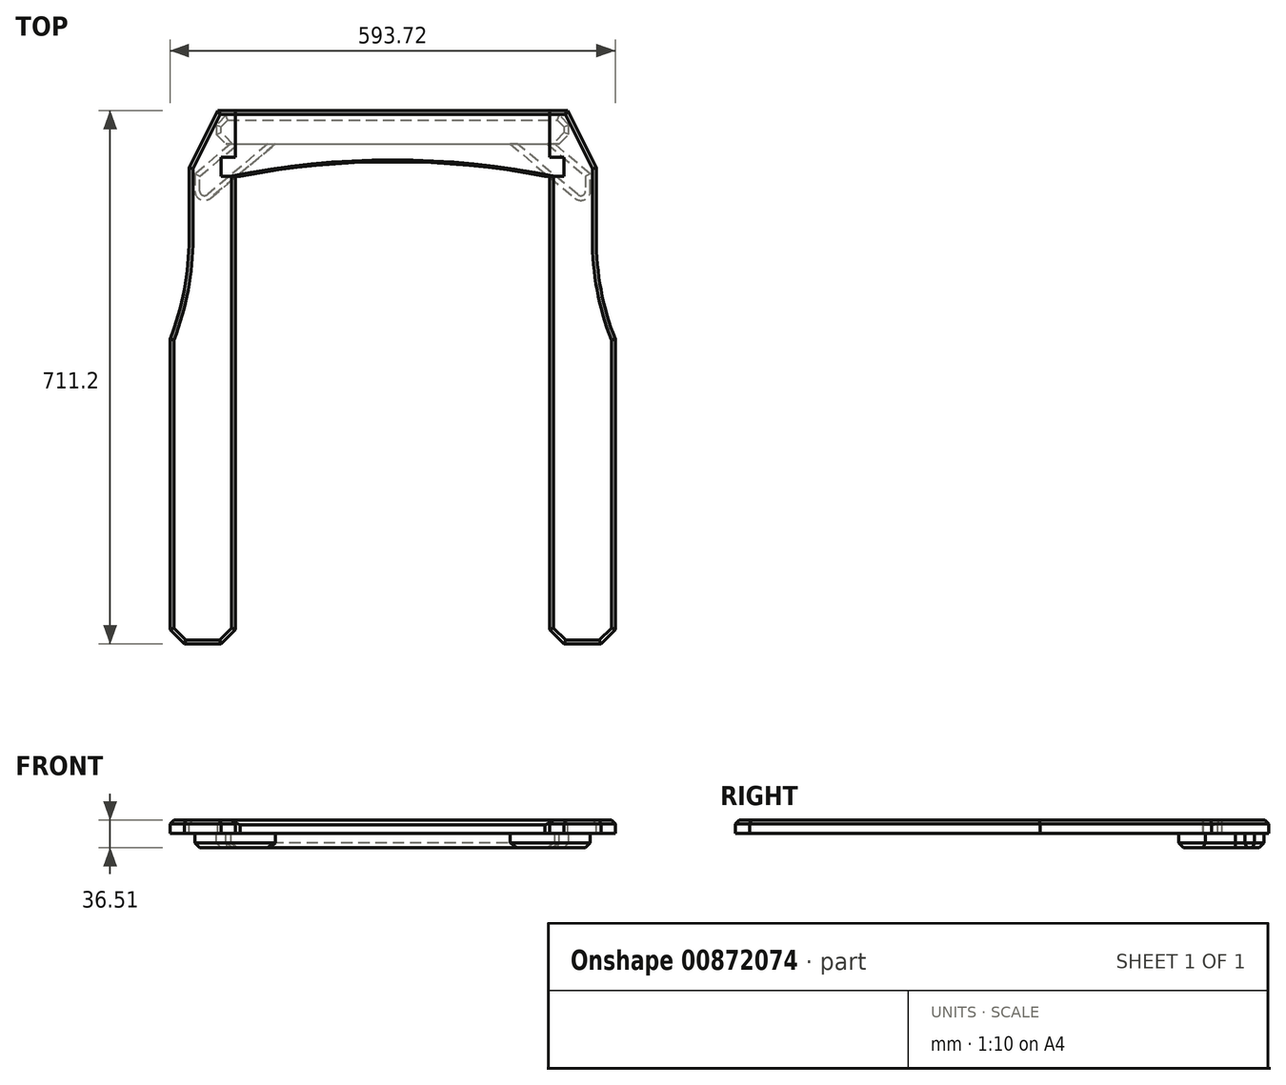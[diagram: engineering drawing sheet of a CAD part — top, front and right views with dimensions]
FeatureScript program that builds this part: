
annotation { "Feature Type Name" : "Feature", "Feature Type Description" : "" }
export const myFeature = defineFeature(function(context is Context, id is Id, definition is map)
    precondition{}
    {
        {
            var Q0;
            Q0=qCreatedBy(makeId("Top.planeOp"),FACE);
            var sketch = newSketch(context, id + "F0", { "sketchPlane" : qUnion([Q0])});
            skLineSegment(sketch, "E0.bottom", {"start": v(0, 0) * mm, "end": v(25.4, 0) * mm});
            skLineSegment(sketch, "E1", {"start": v(25.4, 18.53) * mm, "end": v(25.4, 0.79) * mm, "construction": true});
            skLineSegment(sketch, "E2", {"start": v(431.8, 17.8) * mm, "end": v(431.8, 0) * mm, "construction": true});
            skLineSegment(sketch, "E3", {"start": v(25.4, 0.79) * mm, "end": v(25.4, -24.2) * mm, "construction": true});
            skLineSegment(sketch, "E4", {"start": v(431.8, 0) * mm, "end": v(431.8, -25.28) * mm, "construction": true});
            skLineSegment(sketch, "E5", {"start": v(25.4, 0) * mm, "end": v(431.8, 0) * mm, "construction": true});
            skLineSegment(sketch, "E6", {"start": v(431.8, 0) * mm, "end": v(457.2, 0) * mm});
            skLineSegment(sketch, "E7", {"start": v(228.6, 19.05) * mm, "end": v(228.6, 0) * mm, "construction": true});
            skPoint(sketch, "E7.startSnap0", {"position": v(228.6, 0) * mm});
            skArc(sketch, "E8", {"start": v(431.8, 0) * mm, "mid": v(228.6, 19.05) * mm, "end": v(25.4, 0) * mm});
            skLineSegment(sketch, "E9", {"start": v(0, 0) * mm, "end": v(0, 25.4) * mm});
            skLineSegment(sketch, "E10", {"start": v(0, 25.4) * mm, "end": v(19.05, 25.4) * mm});
            skLineSegment(sketch, "E11", {"start": v(19.05, 25.4) * mm, "end": v(19.05, 87.31) * mm});
            skLineSegment(sketch, "E12", {"start": v(19.05, 87.31) * mm, "end": v(438.15, 87.31) * mm});
            skLineSegment(sketch, "E13", {"start": v(438.15, 87.31) * mm, "end": v(438.15, 25.4) * mm});
            skLineSegment(sketch, "E14", {"start": v(438.15, 25.4) * mm, "end": v(457.2, 25.4) * mm});
            skLineSegment(sketch, "E15", {"start": v(457.2, 25.4) * mm, "end": v(457.2, 0) * mm});
            skSolve(sketch);
        }
        {
            var Q0;
            Q0=qSketchRegion(id+"F0",true);
            extrude(context, id + "F1", {"entities" : qUnion([Q0]), "depth" : 17.46 * mm});
        }
        {
            var Q0;
            Q0=makeQuery(id+"F1.opExtrude","CAP_EDGE",EDGE,{"disambiguationData":[OSD([sQuery(id+"F0.wireOp",EDGE,"E8")])],"isStart":false});
            chamfer(context, id + "F2", {"entities" : qUnion([Q0]), "chamferType" : ChamferType.TWO_OFFSETS, "width1" : 6.35 * mm, "oppositeDirection" : false, "width2" : 2.54 * mm, "tangentPropagation" : true});
        }
        {
            var Q0;
            Q0=makeQuery(id+"F1.opExtrude","CAP_FACE",FACE,{"disambiguationData":[OSD([sQuery(id+"F0.wireOp",EDGE,"E0.bottom"),sQuery(id+"F0.wireOp",EDGE,"E6"),sQuery(id+"F0.wireOp",EDGE,"E8"),sQuery(id+"F0.wireOp",EDGE,"E9"),sQuery(id+"F0.wireOp",EDGE,"E10"),sQuery(id+"F0.wireOp",EDGE,"E11"),sQuery(id+"F0.wireOp",EDGE,"E12"),sQuery(id+"F0.wireOp",EDGE,"E13"),sQuery(id+"F0.wireOp",EDGE,"E14"),sQuery(id+"F0.wireOp",EDGE,"E15")])],"isStart":false});
            var sketch = newSketch(context, id + "F3", { "sketchPlane" : qUnion([Q0])});
            skLineSegment(sketch, "E16", {"start": v(228.6, 119.18) * mm, "end": v(228.6, -123.03) * mm, "construction": true});
            skPoint(sketch, "E16.startSnap0", {"position": v(228.6, 87.31) * mm});
            skLineSegment(sketch, "E17", {"start": v(-4.76, 87.31) * mm, "end": v(-42.86, 11.11) * mm});
            skLineSegment(sketch, "E18", {"start": v(-42.86, 11.11) * mm, "end": v(-42.86, -83.27) * mm});
            skLineSegment(sketch, "E19", {"start": v(19.05, 25.4) * mm, "end": v(0, 25.4) * mm});
            skLineSegment(sketch, "E20", {"start": v(0, 25.4) * mm, "end": v(0, 0) * mm});
            skLineSegment(sketch, "E21", {"start": v(0, 0) * mm, "end": v(19.05, 0) * mm});
            skLineSegment(sketch, "E22", {"start": v(19.05, 87.31) * mm, "end": v(-4.76, 87.31) * mm});
            skLineSegment(sketch, "E23", {"start": v(19.05, 87.31) * mm, "end": v(19.05, 25.4) * mm});
            skLineSegment(sketch, "E24", {"start": v(19.05, 0) * mm, "end": v(19.05, -604.84) * mm});
            skLineSegment(sketch, "E25", {"start": v(-68.26, -604.84) * mm, "end": v(-49.21, -623.89) * mm});
            skLineSegment(sketch, "E26", {"start": v(-49.21, -623.89) * mm, "end": v(0, -623.89) * mm});
            skLineSegment(sketch, "E27", {"start": v(0, -623.89) * mm, "end": v(19.05, -604.84) * mm});
            skLineSegment(sketch, "E28", {"start": v(-68.26, -217.49) * mm, "end": v(-34.9, -217.49) * mm, "construction": true});
            skArc(sketch, "E29", {"start": v(-68.26, -217.49) * mm, "mid": v(-49.27, -151.57) * mm, "end": v(-42.86, -83.27) * mm});
            skLineSegment(sketch, "E30", {"start": v(-68.26, -217.49) * mm, "end": v(-68.26, -604.84) * mm});
            skLineSegment(sketch, "E31.MirrorCS", {"start": v(457.2, 0) * mm, "end": v(438.15, 0) * mm});
            skLineSegment(sketch, "E32.MirrorCS", {"start": v(457.2, 25.4) * mm, "end": v(457.2, 0) * mm});
            skLineSegment(sketch, "E33.MirrorCS", {"start": v(525.46, -604.84) * mm, "end": v(506.41, -623.89) * mm});
            skLineSegment(sketch, "E34.MirrorCS", {"start": v(457.2, -623.89) * mm, "end": v(438.15, -604.84) * mm});
            skLineSegment(sketch, "E35.MirrorCS", {"start": v(461.96, 87.31) * mm, "end": v(500.06, 11.11) * mm});
            skLineSegment(sketch, "E36.MirrorCS", {"start": v(438.15, 25.4) * mm, "end": v(457.2, 25.4) * mm});
            skLineSegment(sketch, "E37.MirrorCS", {"start": v(438.15, 87.31) * mm, "end": v(438.15, 25.4) * mm});
            skLineSegment(sketch, "E38.MirrorCS", {"start": v(438.15, 0) * mm, "end": v(438.15, -604.84) * mm});
            skLineSegment(sketch, "E39.MirrorCS", {"start": v(438.15, 87.31) * mm, "end": v(461.96, 87.31) * mm});
            skLineSegment(sketch, "E40.MirrorCS", {"start": v(500.06, 11.11) * mm, "end": v(500.06, -83.27) * mm});
            skLineSegment(sketch, "E41.MirrorCS", {"start": v(525.46, -217.49) * mm, "end": v(492.1, -217.49) * mm, "construction": true});
            skLineSegment(sketch, "E42.MirrorCS", {"start": v(506.41, -623.89) * mm, "end": v(457.2, -623.89) * mm});
            skLineSegment(sketch, "E43.MirrorCS", {"start": v(525.46, -217.49) * mm, "end": v(525.46, -604.84) * mm});
            skArc(sketch, "E44.MirrorCS", {"start": v(525.46, -217.49) * mm, "mid": v(506.47, -151.57) * mm, "end": v(500.06, -83.27) * mm});
            skSolve(sketch);
        }
        {
            var Q0;
            Q0=qSketchRegion(id+"F3",true);
            extrude(context, id + "F4", {"entities" : qUnion([Q0]), "depth" : -17.46 * mm});
        }
        {
            var Q0;
            Q0=makeQuery(id+"F1.opExtrude","CAP_EDGE",EDGE,{"disambiguationData":[OSD([sQuery(id+"F0.wireOp",EDGE,"E12")])],"isStart":false});
            var Q1;
            Q1=makeQuery(id+"F4.opExtrude","CAP_EDGE",EDGE,{"disambiguationData":[OSD([sQuery(id+"F3.wireOp",EDGE,"E22")])],"isStart":true});
            var Q2;
            Q2=makeQuery(id+"F4.opExtrude","CAP_EDGE",EDGE,{"disambiguationData":[OSD([sQuery(id+"F3.wireOp",EDGE,"E17")])],"isStart":true});
            var Q3;
            Q3=makeQuery(id+"F4.opExtrude","CAP_EDGE",EDGE,{"disambiguationData":[OSD([sQuery(id+"F3.wireOp",EDGE,"E18")])],"isStart":true});
            var Q4;
            Q4=makeQuery(id+"F4.opExtrude","CAP_EDGE",EDGE,{"disambiguationData":[OSD([sQuery(id+"F3.wireOp",EDGE,"E30")])],"isStart":true});
            var Q5;
            Q5=makeQuery(id+"F4.opExtrude","CAP_EDGE",EDGE,{"disambiguationData":[OSD([sQuery(id+"F3.wireOp",EDGE,"E25")])],"isStart":true});
            var Q6;
            Q6=makeQuery(id+"F4.opExtrude","CAP_EDGE",EDGE,{"disambiguationData":[OSD([sQuery(id+"F3.wireOp",EDGE,"E26")])],"isStart":true});
            var Q7;
            Q7=makeQuery(id+"F4.opExtrude","CAP_EDGE",EDGE,{"disambiguationData":[OSD([sQuery(id+"F3.wireOp",EDGE,"E27")])],"isStart":true});
            var Q8;
            Q8=makeQuery(id+"F4.opExtrude","CAP_EDGE",EDGE,{"disambiguationData":[OSD([sQuery(id+"F3.wireOp",EDGE,"E24")])],"isStart":true});
            var Q9;
            Q9=makeQuery(id+"F4.opExtrude","CAP_EDGE",EDGE,{"disambiguationData":[OSD([sQuery(id+"F3.wireOp",EDGE,"E39.MirrorCS")])],"isStart":true});
            var Q10;
            Q10=makeQuery(id+"F4.opExtrude","CAP_EDGE",EDGE,{"disambiguationData":[OSD([sQuery(id+"F3.wireOp",EDGE,"E35.MirrorCS")])],"isStart":true});
            var Q11;
            Q11=makeQuery(id+"F4.opExtrude","CAP_EDGE",EDGE,{"disambiguationData":[OSD([sQuery(id+"F3.wireOp",EDGE,"E40.MirrorCS")])],"isStart":true});
            var Q12;
            Q12=makeQuery(id+"F4.opExtrude","CAP_EDGE",EDGE,{"disambiguationData":[OSD([sQuery(id+"F3.wireOp",EDGE,"E44.MirrorCS")])],"isStart":true});
            var Q13;
            Q13=makeQuery(id+"F4.opExtrude","CAP_EDGE",EDGE,{"disambiguationData":[OSD([sQuery(id+"F3.wireOp",EDGE,"E43.MirrorCS")])],"isStart":true});
            var Q14;
            Q14=makeQuery(id+"F4.opExtrude","CAP_EDGE",EDGE,{"disambiguationData":[OSD([sQuery(id+"F3.wireOp",EDGE,"E33.MirrorCS")])],"isStart":true});
            var Q15;
            Q15=makeQuery(id+"F4.opExtrude","CAP_EDGE",EDGE,{"disambiguationData":[OSD([sQuery(id+"F3.wireOp",EDGE,"E42.MirrorCS")])],"isStart":true});
            var Q16;
            Q16=makeQuery(id+"F4.opExtrude","CAP_EDGE",EDGE,{"disambiguationData":[OSD([sQuery(id+"F3.wireOp",EDGE,"E34.MirrorCS")])],"isStart":true});
            var Q17;
            Q17=makeQuery(id+"F4.opExtrude","CAP_EDGE",EDGE,{"disambiguationData":[OSD([sQuery(id+"F3.wireOp",EDGE,"E38.MirrorCS")])],"isStart":true});
            chamfer(context, id + "F5", {"entities" : qUnion([Q0, Q1, Q2, Q3, Q4, Q5, Q6, Q7, Q8, Q9, Q10, Q11, Q12, Q13, Q14, Q15, Q16, Q17]), "width" : 5.08 * mm, "tangentPropagation" : true});
        }
        {
            var Q0;
            Q0=makeQuery(id+"F1.opExtrude","CAP_FACE",FACE,{"disambiguationData":[OSD([sQuery(id+"F0.wireOp",EDGE,"E0.bottom"),sQuery(id+"F0.wireOp",EDGE,"E6"),sQuery(id+"F0.wireOp",EDGE,"E8"),sQuery(id+"F0.wireOp",EDGE,"E9"),sQuery(id+"F0.wireOp",EDGE,"E10"),sQuery(id+"F0.wireOp",EDGE,"E11"),sQuery(id+"F0.wireOp",EDGE,"E12"),sQuery(id+"F0.wireOp",EDGE,"E13"),sQuery(id+"F0.wireOp",EDGE,"E14"),sQuery(id+"F0.wireOp",EDGE,"E15")])],"isStart":true});
            var sketch = newSketch(context, id + "F6", { "sketchPlane" : qUnion([Q0])});
            skLineSegment(sketch, "E45", {"start": v(450.85, -80.96) * mm, "end": v(6.35, -80.96) * mm});
            skLineSegment(sketch, "E46", {"start": v(-6.35, -68.26) * mm, "end": v(-6.35, -55.56) * mm});
            skLineSegment(sketch, "E47", {"start": v(6.35, -42.86) * mm, "end": v(450.85, -42.86) * mm});
            skLineSegment(sketch, "E48", {"start": v(463.55, -55.56) * mm, "end": v(463.55, -68.26) * mm});
            skLineSegment(sketch, "E49", {"start": v(450.85, -80.96) * mm, "end": v(463.55, -68.26) * mm});
            skLineSegment(sketch, "E50", {"start": v(-6.35, -68.26) * mm, "end": v(6.35, -80.96) * mm});
            skLineSegment(sketch, "E51", {"start": v(450.85, -42.86) * mm, "end": v(463.55, -55.56) * mm});
            skLineSegment(sketch, "E52", {"start": v(-6.35, -55.56) * mm, "end": v(6.35, -42.86) * mm});
            skSolve(sketch);
        }
        {
            var Q0;
            Q0=qSketchRegion(id+"F6",true);
            extrude(context, id + "F7", {"entities" : qUnion([Q0]), "depth" : 19.05 * mm});
        }
        {
            var Q0;
            Q0=makeQuery(id+"F7.opExtrude","CAP_FACE",FACE,{"disambiguationData":[OSD([sQuery(id+"F6.wireOp",EDGE,"E45"),sQuery(id+"F6.wireOp",EDGE,"E46"),sQuery(id+"F6.wireOp",EDGE,"E47"),sQuery(id+"F6.wireOp",EDGE,"E48"),sQuery(id+"F6.wireOp",EDGE,"E49")])],"isStart":false});
            var sketch = newSketch(context, id + "F8", { "sketchPlane" : qUnion([Q0])});
            skLineSegment(sketch, "E53", {"start": v(385.23, -42.86) * mm, "end": v(471.38, 29.43) * mm});
            skLineSegment(sketch, "E54", {"start": v(492.24, 19.7) * mm, "end": v(492.24, -2.8) * mm});
            skLineSegment(sketch, "E55", {"start": v(492.24, -2.8) * mm, "end": v(444.5, -42.86) * mm});
            skLineSegment(sketch, "E56", {"start": v(444.5, -42.86) * mm, "end": v(385.23, -42.86) * mm});
            skLineSegment(sketch, "E57", {"start": v(228.6, -80.96) * mm, "end": v(228.6, -42.86) * mm, "construction": true});
            skLineSegment(sketch, "E58.MirrorCS", {"start": v(-35.04, -2.8) * mm, "end": v(12.7, -42.86) * mm});
            skLineSegment(sketch, "E59.MirrorCS", {"start": v(12.7, -42.86) * mm, "end": v(71.97, -42.86) * mm});
            skLineSegment(sketch, "E60.MirrorCS", {"start": v(71.97, -42.86) * mm, "end": v(-14.18, 29.43) * mm});
            skLineSegment(sketch, "E61.MirrorCS", {"start": v(-35.04, 19.7) * mm, "end": v(-35.04, -2.8) * mm});
            skPoint(sketch, "E62.visualSharp", {"position": v(492.24, 46.93) * mm});
            skArc(sketch, "E62.filletArc", {"start": v(492.24, 19.7) * mm, "mid": v(484.91, 31.2) * mm, "end": v(471.38, 29.43) * mm});
            skArc(sketch, "E63.MirrorCS", {"start": v(-35.04, 19.7) * mm, "mid": v(-27.71, 31.2) * mm, "end": v(-14.18, 29.43) * mm});
            skLineSegment(sketch, "E64", {"start": v(492.24, 19.7) * mm, "end": v(492.24, 46.93) * mm, "construction": true});
            skLineSegment(sketch, "E65", {"start": v(492.24, 46.93) * mm, "end": v(471.38, 29.43) * mm, "construction": true});
            skSolve(sketch);
        }
        {
            var Q0;
            Q0=qSketchRegion(id+"F8",true);
            extrude(context, id + "F9", {"entities" : qUnion([Q0]), "depth" : -19.05 * mm});
        }
        {
            var Q0;
            Q0=makeQuery(id+"F9.opExtrude","CAP_EDGE",EDGE,{"disambiguationData":[OSD([sQuery(id+"F8.wireOp",EDGE,"E55")])],"isStart":true});
            var Q1;
            Q1=makeQuery(id+"F9.opExtrude","CAP_EDGE",EDGE,{"disambiguationData":[OSD([sQuery(id+"F8.wireOp",EDGE,"E54")])],"isStart":true});
            var Q2;
            Q2=makeQuery(id+"F9.opExtrude","CAP_EDGE",EDGE,{"disambiguationData":[OSD([sQuery(id+"F8.wireOp",EDGE,"E62.filletArc")])],"isStart":true});
            var Q3;
            Q3=makeQuery(id+"F9.opExtrude","CAP_EDGE",EDGE,{"disambiguationData":[OSD([sQuery(id+"F8.wireOp",EDGE,"E60.MirrorCS")])],"isStart":true});
            var Q4;
            Q4=makeQuery(id+"F9.opExtrude","CAP_EDGE",EDGE,{"disambiguationData":[OSD([sQuery(id+"F8.wireOp",EDGE,"E63.MirrorCS")])],"isStart":true});
            var Q5;
            Q5=makeQuery(id+"F9.opExtrude","CAP_EDGE",EDGE,{"disambiguationData":[OSD([sQuery(id+"F8.wireOp",EDGE,"E58.MirrorCS")])],"isStart":true});
            var Q6;
            Q6=makeQuery(id+"F7.opExtrude","CAP_EDGE",EDGE,{"disambiguationData":[OSD([sQuery(id+"F6.wireOp",EDGE,"E46")])],"isStart":false});
            var Q7;
            Q7=makeQuery(id+"F7.opExtrude","CAP_EDGE",EDGE,{"disambiguationData":[OSD([sQuery(id+"F6.wireOp",EDGE,"E50")])],"isStart":false});
            var Q8;
            Q8=makeQuery(id+"F7.opExtrude","CAP_EDGE",EDGE,{"disambiguationData":[OSD([sQuery(id+"F6.wireOp",EDGE,"E45")])],"isStart":false});
            var Q9;
            Q9=makeQuery(id+"F7.opExtrude","CAP_EDGE",EDGE,{"disambiguationData":[OSD([sQuery(id+"F6.wireOp",EDGE,"E49")])],"isStart":false});
            var Q10;
            Q10=makeQuery(id+"F7.opExtrude","CAP_EDGE",EDGE,{"disambiguationData":[OSD([sQuery(id+"F6.wireOp",EDGE,"E48")])],"isStart":false});
            var Q11;
            Q11=makeQuery(id+"F7.opExtrude","CAP_EDGE",EDGE,{"disambiguationData":[OSD([sQuery(id+"F6.wireOp",EDGE,"E51")])],"isStart":false});
            var Q12;
            Q12=makeQuery(id+"F7.opExtrude","CAP_EDGE",EDGE,{"disambiguationData":[OSD([sQuery(id+"F6.wireOp",EDGE,"E52")])],"isStart":false});
            chamfer(context, id + "F10", {"entities" : qUnion([Q0, Q1, Q2, Q3, Q4, Q5, Q6, Q7, Q8, Q9, Q10, Q11, Q12]), "width" : 6.35 * mm, "tangentPropagation" : true});
        }
    });
